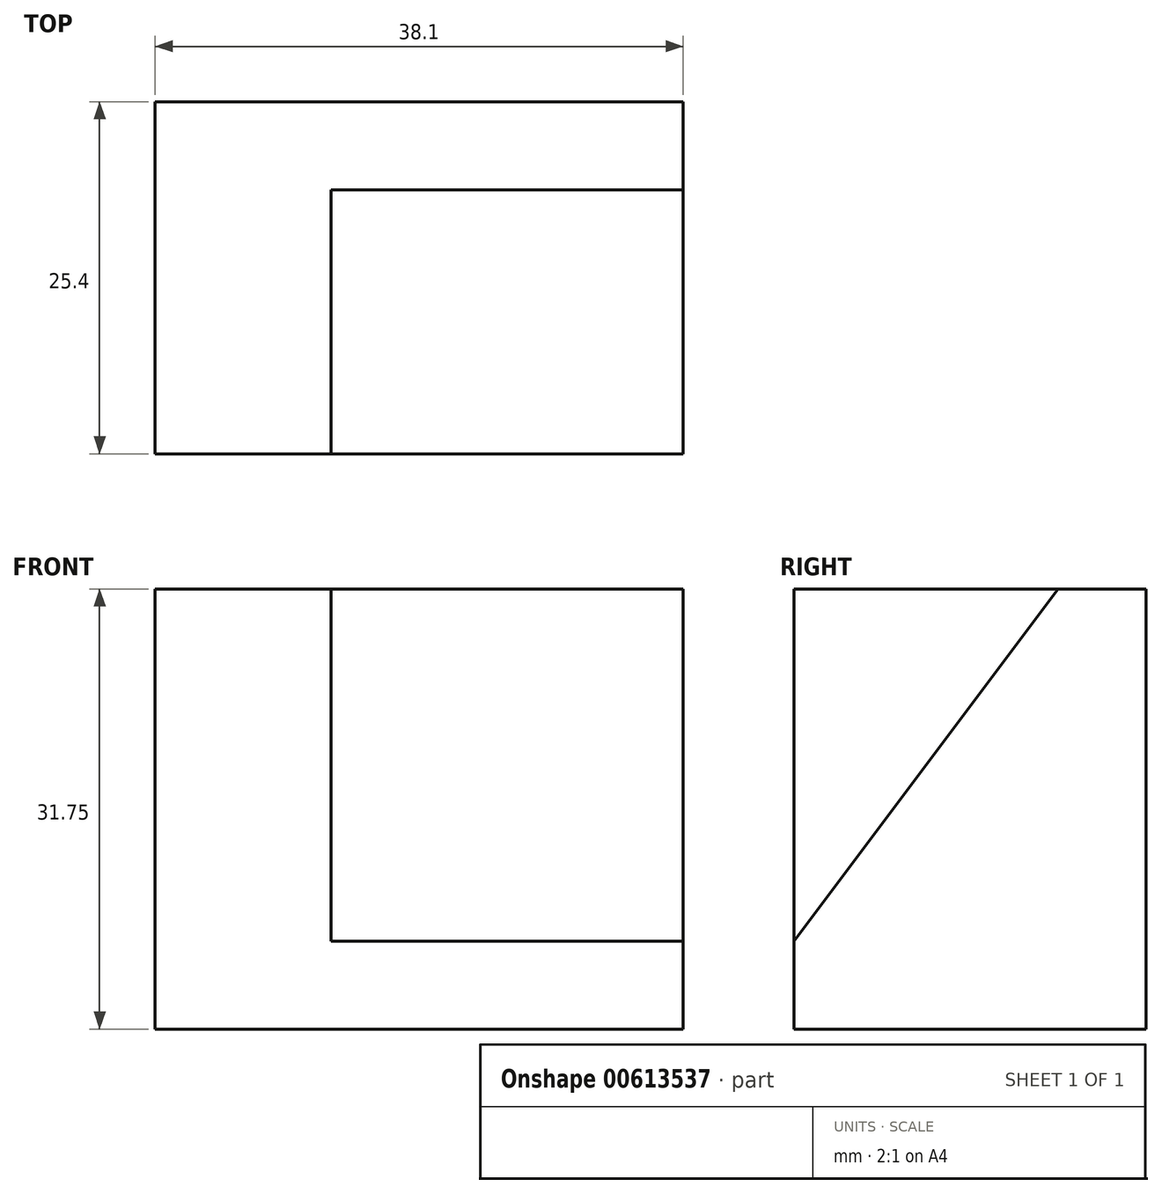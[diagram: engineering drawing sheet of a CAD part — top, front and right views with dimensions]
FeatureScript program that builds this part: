
annotation { "Feature Type Name" : "Feature", "Feature Type Description" : "" }
export const myFeature = defineFeature(function(context is Context, id is Id, definition is map)
    precondition{}
    {
        {
            var Q0;
            Q0=qCreatedBy(makeId("Front.planeOp"),FACE);
            var sketch = newSketch(context, id + "F0", { "sketchPlane" : qUnion([Q0])});
            skLineSegment(sketch, "E0.bottom", {"start": v(0, 0) * mm, "end": v(38.1, 0) * mm});
            skLineSegment(sketch, "E0.top", {"start": v(0, 31.75) * mm, "end": v(38.1, 31.75) * mm});
            skLineSegment(sketch, "E0.left", {"start": v(0, 0) * mm, "end": v(0, 31.75) * mm});
            skLineSegment(sketch, "E0.right", {"start": v(38.1, 0) * mm, "end": v(38.1, 31.75) * mm});
            skSolve(sketch);
        }
        {
            var Q0;
            Q0=makeQuery(id+"F0.imprint","IMPRINT",FACE,{"disambiguationData":[TD([[makeQuery(id+"F0.imprint","IMPRINT",EDGE,{"derivedFrom":sQuery(id+"F0.wireOp",EDGE,"E0.bottom")}),1.0]])]});
            extrude(context, id + "F1", {"entities" : qUnion([Q0]), "depth" : 25.4 * mm, "offsetDistance" : 25.4 * mm});
        }
        {
            var Q0;
            Q0=makeQuery(id+"F1.opExtrude","SWEPT_FACE",FACE,{"disambiguationData":[OSD([sQuery(id+"F0.wireOp",EDGE,"E0.right")])]});
            var sketch = newSketch(context, id + "F2", { "sketchPlane" : qUnion([Q0])});
            skLineSegment(sketch, "E1", {"start": v(0, 31.75) * mm, "end": v(-6.35, 31.75) * mm});
            skLineSegment(sketch, "E2", {"start": v(-25.4, 0) * mm, "end": v(-25.4, 6.35) * mm});
            skLineSegment(sketch, "E3", {"start": v(-25.4, 6.35) * mm, "end": v(-6.35, 31.75) * mm});
            skSolve(sketch);
        }
        {
            var Q0;
            {var subQ0=sQuery(id+"F2.wireOp",EDGE,"E3");Q0=makeQuery(id+"F2.imprint","IMPRINT",FACE,{"disambiguationData":[TD([[makeQuery(id+"F2.imprint","IMPRINT",EDGE,{"derivedFrom":subQ0}),1.0]])]});}
            extrude(context, id + "F3", {"entities" : qUnion([Q0]), "operationType" : NewBodyOperationType.REMOVE, "oppositeDirection" : true, "depth" : 25.4 * mm, "offsetDistance" : 25.4 * mm});
        }
    });
